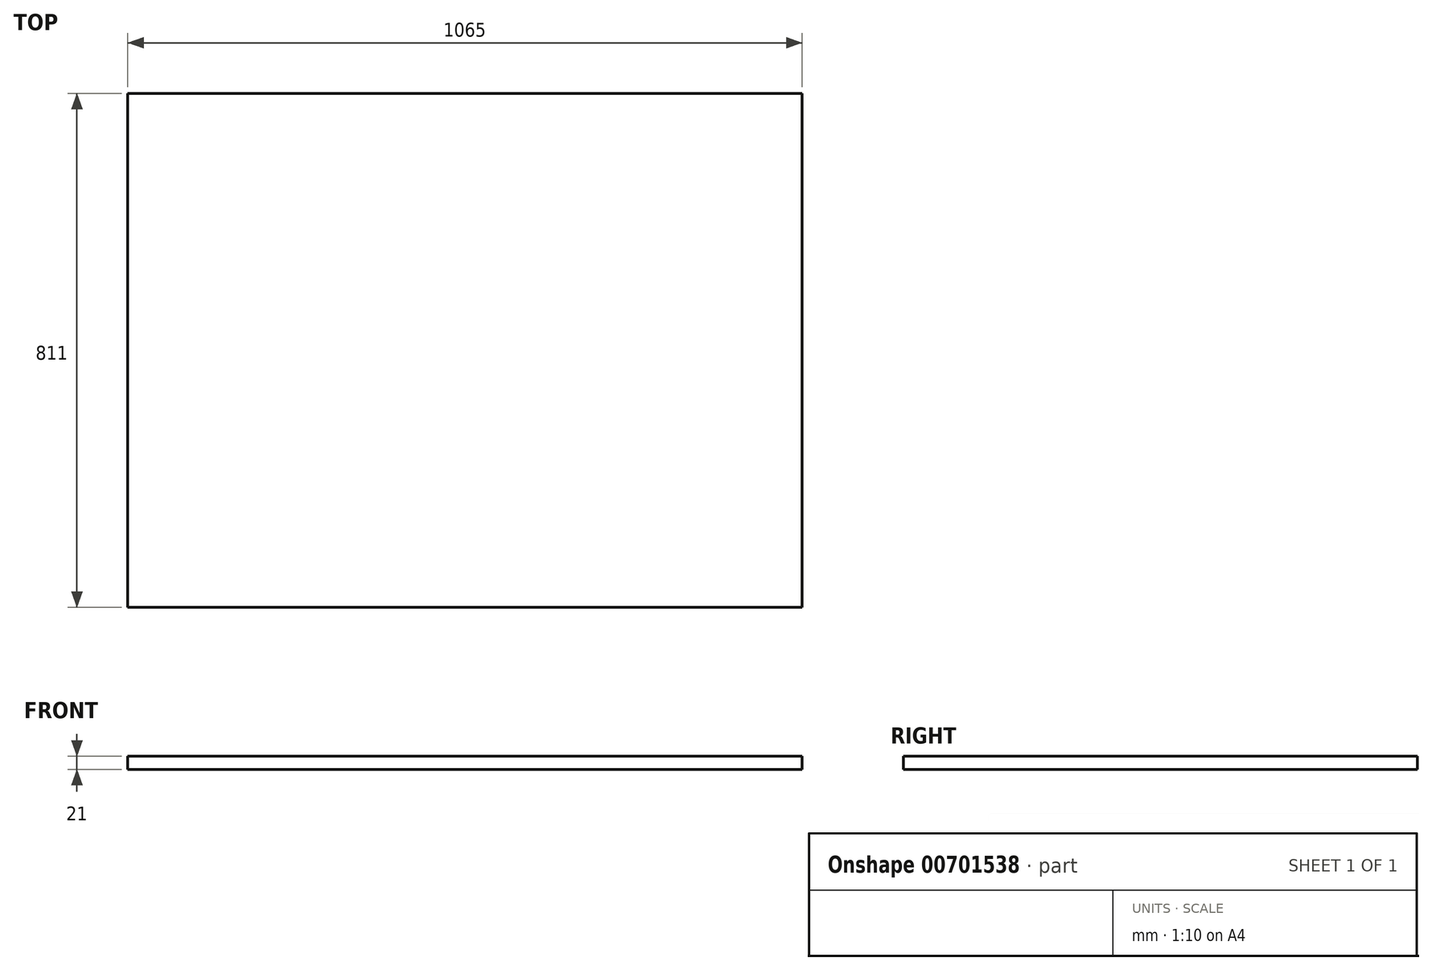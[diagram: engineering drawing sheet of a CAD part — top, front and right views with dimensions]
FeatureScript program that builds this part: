
annotation { "Feature Type Name" : "Feature", "Feature Type Description" : "" }
export const myFeature = defineFeature(function(context is Context, id is Id, definition is map)
    precondition{}
    {
        {
            var Q0;
            Q0=qCreatedBy(makeId("Top.planeOp"),FACE);
            var sketch = newSketch(context, id + "F0", { "sketchPlane" : qUnion([Q0])});
            skLineSegment(sketch, "E0.bottom", {"start": v(-532.5, 405.5) * mm, "end": v(532.5, 405.5) * mm});
            skLineSegment(sketch, "E0.top", {"start": v(-532.5, -405.5) * mm, "end": v(532.5, -405.5) * mm});
            skLineSegment(sketch, "E0.left", {"start": v(-532.5, 405.5) * mm, "end": v(-532.5, -405.5) * mm});
            skLineSegment(sketch, "E0.right", {"start": v(532.5, 405.5) * mm, "end": v(532.5, -405.5) * mm});
            skPoint(sketch, "E0.middle", {"position": v(0, 0) * mm});
            skSolve(sketch);
        }
        {
            var Q0;
            Q0=makeQuery(id+"F0.imprint","IMPRINT",FACE,{"disambiguationData":[TD([[makeQuery(id+"F0.imprint","IMPRINT",EDGE,{"derivedFrom":sQuery(id+"F0.wireOp",EDGE,"E0.bottom")}),-1.0]])]});
            extrude(context, id + "F1", {"entities" : qUnion([Q0]), "depth" : 21 * mm, "offsetDistance" : 25 * mm});
        }
    });
